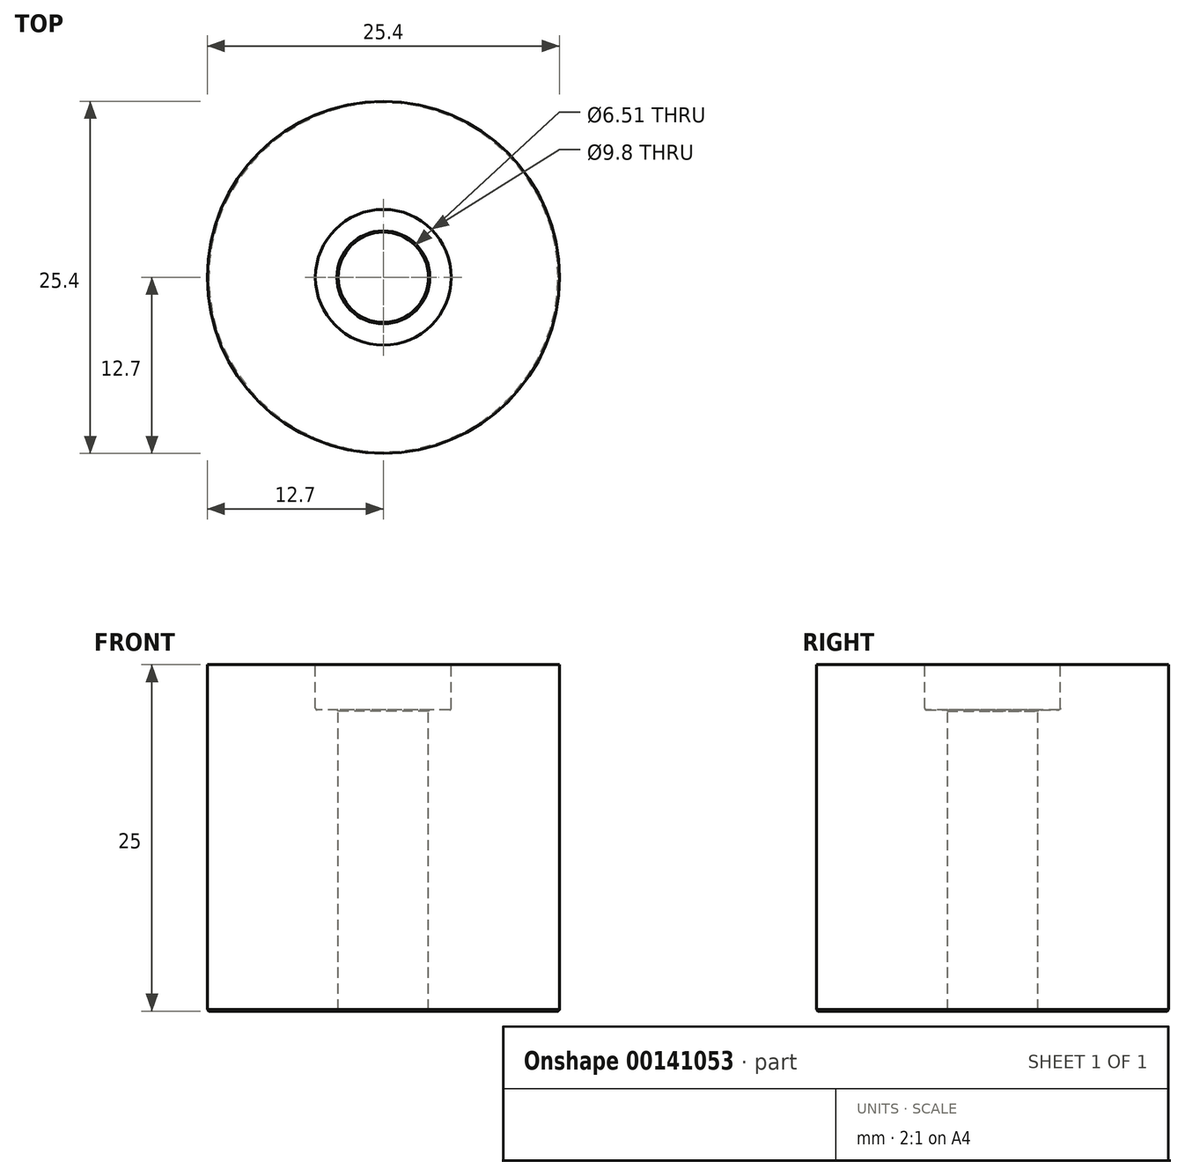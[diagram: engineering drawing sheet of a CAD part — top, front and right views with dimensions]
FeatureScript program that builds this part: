
annotation { "Feature Type Name" : "Feature", "Feature Type Description" : "" }
export const myFeature = defineFeature(function(context is Context, id is Id, definition is map)
    precondition{}
    {
        {
            var Q0;
            Q0=qCreatedBy(makeId("Top.planeOp"),FACE);
            var sketch = newSketch(context, id + "F0", { "sketchPlane" : qUnion([Q0])});
            skCircle(sketch, "E0", {"center": v(0, 0) * mm, "radius": 12.7 * mm});
            skCircle(sketch, "E1", {"center": v(0, 0) * mm, "radius": 3.25 * mm});
            skSolve(sketch);
        }
        {
            var Q0;
            Q0 = qSketchRegion(id + "F0", true);
            extrude(context, id + "F1", {"entities" : qUnion([Q0]), "oppositeDirection" : true, "depth" : 25 * mm});
        }
        {
            var Q0;
            Q0=makeQuery(id+"F1.opExtrude","CAP_FACE",FACE,{"disambiguationData":[OSD([sQuery(id+"F0.wireOp",EDGE,"E0"),sQuery(id+"F0.wireOp",EDGE,"E1")])],"isStart":true});
            var sketch = newSketch(context, id + "F2", { "sketchPlane" : qUnion([Q0])});
            skCircle(sketch, "E2", {"center": v(0, 0) * mm, "radius": 4.9 * mm});
            skSolve(sketch);
        }
        {
            var Q0;
            Q0 = qSketchRegion(id + "F2", true);
            extrude(context, id + "F3", {"entities" : qUnion([Q0]), "operationType" : NewBodyOperationType.REMOVE, "oppositeDirection" : true, "depth" : 3.25 * mm});
        }
        {
            var Q0;
            Q0=makeQuery(id+"F3.boolean.opBoolean","COPY",EDGE,{"derivedFrom":makeQuery(id+"F3.opExtrude","CAP_EDGE",EDGE,{"disambiguationData":[OSD([sQuery(id+"F2.wireOp",EDGE,"E2")])],"isStart":false})});
            fillet(context, id + "F4", {"entities" : qUnion([Q0]), "radius" : .1 * mm, "tangentPropagation" : true, "allowEdgeOverflow" : false});
        }
        {
            var Q0;
            Q0=makeQuery(id+"F3.boolean.opBoolean","INTERSECT",EDGE,{"derivedFrom":[makeQuery(id+"F1.opExtrude","SWEPT_FACE",FACE,{"disambiguationData":[OSD([sQuery(id+"F0.wireOp",EDGE,"E1")])]}),makeQuery(id+"F3.opExtrude","CAP_FACE",FACE,{"disambiguationData":[OSD([sQuery(id+"F2.wireOp",EDGE,"E2")])],"isStart":false})]});
            var Q1;
            Q1=makeQuery(id+"F3.boolean.opBoolean","COPY",EDGE,{"derivedFrom":makeQuery(id+"F3.opExtrude","CAP_EDGE",EDGE,{"disambiguationData":[OSD([sQuery(id+"F2.wireOp",EDGE,"E2")])],"isStart":true})});
            var Q2;
            Q2=makeQuery(id+"F1.opExtrude","CAP_EDGE",EDGE,{"disambiguationData":[OSD([sQuery(id+"F0.wireOp",EDGE,"E1")])],"isStart":false});
            var Q3;
            Q3=makeQuery(id+"F1.opExtrude","CAP_EDGE",EDGE,{"disambiguationData":[OSD([sQuery(id+"F0.wireOp",EDGE,"E0")])],"isStart":false});
            chamfer(context, id + "F5", {"entities" : qUnion([Q0, Q1, Q2, Q3]), "width" : .1 * mm, "tangentPropagation" : true});
        }
    });
